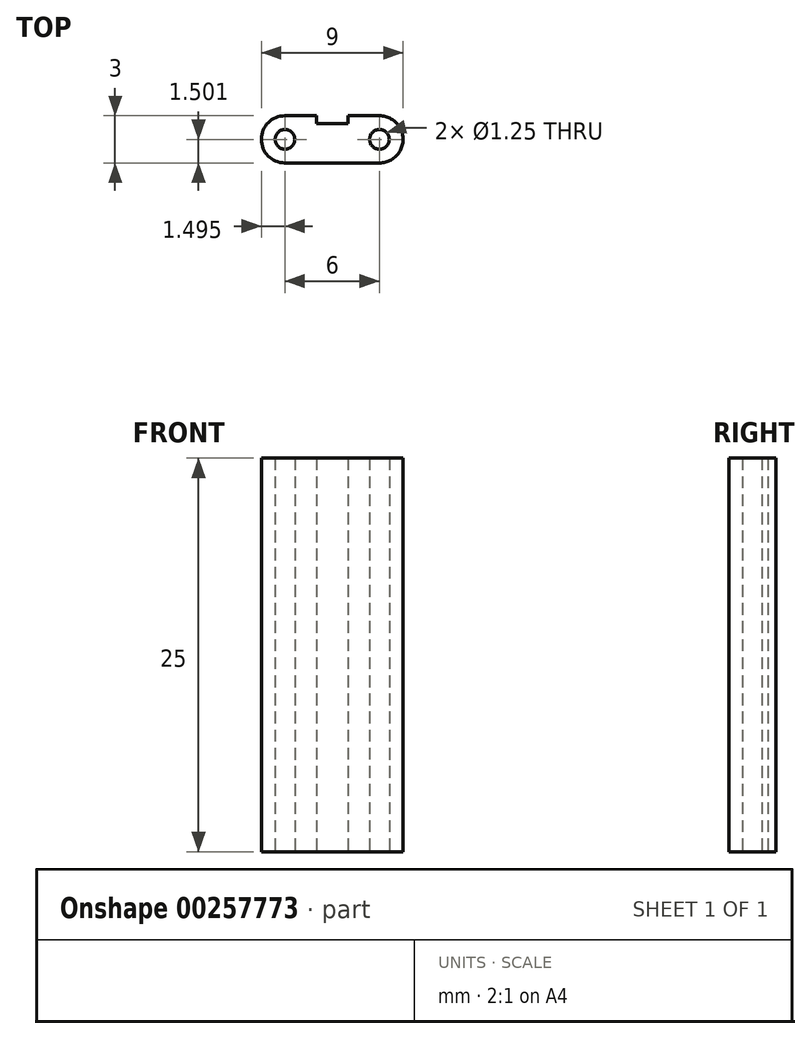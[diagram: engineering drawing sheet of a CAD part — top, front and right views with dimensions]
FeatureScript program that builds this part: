
annotation { "Feature Type Name" : "Feature", "Feature Type Description" : "" }
export const myFeature = defineFeature(function(context is Context, id is Id, definition is map)
    precondition{}
    {
        {
            var Q0;
            Q0=qCreatedBy(makeId("Top.planeOp"),FACE);
            var sketch = newSketch(context, id + "F0", { "sketchPlane" : qUnion([Q0])});
            skLineSegment(sketch, "E0", {"start": v(-46.37, -15.52) * mm, "end": v(-40.37, -15.52) * mm});
            skPoint(sketch, "E1.end.orphan", {"position": v(-46.35, -12.52) * mm});
            skPoint(sketch, "E2.end.orphan", {"position": v(-40.35, -12.52) * mm});
            skLineSegment(sketch, "E3", {"start": v(-46.35, -12.52) * mm, "end": v(-44.35, -12.52) * mm});
            skLineSegment(sketch, "E4", {"start": v(-44.35, -12.52) * mm, "end": v(-44.35, -13.02) * mm});
            skLineSegment(sketch, "E5", {"start": v(-44.35, -13.02) * mm, "end": v(-42.35, -13.02) * mm});
            skLineSegment(sketch, "E6", {"start": v(-42.35, -13.02) * mm, "end": v(-42.35, -12.52) * mm});
            skLineSegment(sketch, "E7", {"start": v(-40.35, -12.52) * mm, "end": v(-42.35, -12.52) * mm});
            skArc(sketch, "E8", {"start": v(-46.35, -12.52) * mm, "mid": v(-47.85, -14.01) * mm, "end": v(-46.37, -15.52) * mm});
            skArc(sketch, "E9", {"start": v(-40.37, -15.52) * mm, "mid": v(-38.85, -14.03) * mm, "end": v(-40.35, -12.52) * mm});
            skCircle(sketch, "E10", {"center": v(-40.35, -14.02) * mm, "radius": 0.62 * mm});
            skCircle(sketch, "E11", {"center": v(-46.35, -14.02) * mm, "radius": 0.62 * mm});
            skSolve(sketch);
        }
        {
            var Q0;
            Q0 = qSketchRegion(id + "F0", true);
            extrude(context, id + "F1", {"entities" : qUnion([Q0]), "depth" : 25 * mm});
        }
    });
